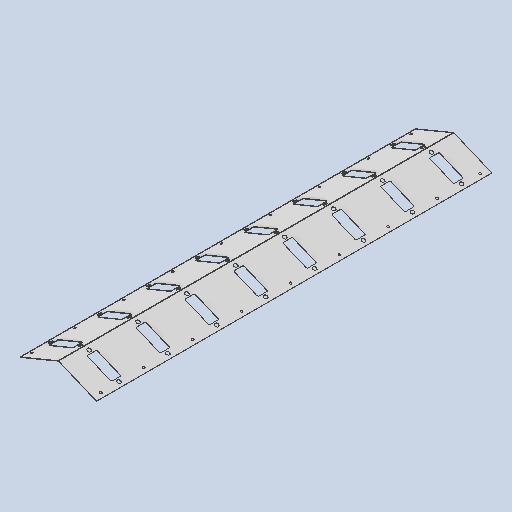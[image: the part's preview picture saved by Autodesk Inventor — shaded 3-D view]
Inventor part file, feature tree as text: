
AUTODESK INVENTOR PART (.ipt)
format: ipt  version: 2025 (Build 290162010, 162A)  size: 736,256 bytes
history: native  units: mm
features: sketch x4, sheet_metal_op x3, extrude x3, other x3, pattern_linear x2, fillet x1, pattern_circular x1, mirror x1, chamfer x1
ambient origin geometry x8: Origin, YZ Plane, XZ Plane, XY Plane, X Axis, Y Axis, Z Axis, Center Point
bodies: Body1 (feature_tree)
feature tree (19):
  sheet_metal_op  "Contour Flange2"
  extrude  "Extrusion5"  Depth=0.9mm
  extrude  "Extrusion7"  Depth=2.0mm
  fillet  "Fillet2"  Radius=2.0mm
  pattern_circular  "Circular Pattern1"  [2 undecoded]
  pattern_linear  "Rectangular Pattern5"  Count1=202  [1 undecoded]
  extrude  "Extrusion8"  Depth=2.0mm
  pattern_linear  "Rectangular Pattern6"  Spacing1=3.0mm  [1 undecoded]
  mirror  "Mirror5"
  other  "Corner Chamfer1"
  chamfer  "Corner Round1"
  sketch  "Sketch1"  dims[d46=513.0mm d47=0.9mm]
  other  "Plate4"
  sheet_metal_op  "Bend4"
  sheet_metal_op  "Corner4"
  sketch  "Sketch12"  dims[d48=4.0mm d49=2.0mm d50=2.0mm]
  sketch  "Sketch14"  dims[d51=1.0mm]
  sketch  "Sketch15"  dims[d52=4.0mm d53=2.0mm d54=2020.0mm d55=2.0mm d56=3.0mm d57=8.0mm d58=2.0mm d59=2.0mm d115=11.0mm d116=189.129mm d117=40.75mm d118=11.0mm d119=189.129mm d120=40.75mm d121=10.0mm d122=0.0mm d131=135.0mm d132=50.0mm d135=125.0mm d136=104.589mm d137=10.0mm d138=0.0mm d139=5.0mm d140=20.0mm d141=45.0deg d143=80.0mm d145=250.0mm d146=11.0mm d147=189.129mm d148=0.0mm d149=0.0mm d150=70.0mm d152=250.0mm d153=2.0mm d154=6.0mm d155=45.0deg d156=2.0mm d160=165.0mm d161=16.8mm d162=16.8mm]
  other  "Definition1"
note: 4 required parameter values undecoded (feature->parameter linkage not recoverable at this tier; creation-order binding heuristic only, values carry confidence <= 0.55)
